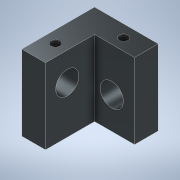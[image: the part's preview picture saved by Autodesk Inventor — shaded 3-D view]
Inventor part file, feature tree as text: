
AUTODESK INVENTOR PART (.ipt)
format: ipt  version: 2021 (Build 250183000, 183)  size: 216,576 bytes
history: native  units: in
note: dims shown in document units (in); Inventor stores cm internally (conversion verified against a paired STEP export)
features: extrude x8, other x8, sketch x3, thread x2, plane x2, chamfer x1, fillet x1, projected_geometry x1
ambient origin geometry x8: Origin, YZ Plane, XZ Plane, XY Plane, X Axis, Y Axis, Z Axis, Center Point
bodies: Solid1 (feature_tree), Body (feature_tree), Solid2 (feature_tree)
feature tree (26):
  extrude  "Extrusion1"  Depth=1.378in
  other  "Lower Galvo Mount"
  other  "Upper Galvo Mount"
  extrude  "Extrusion2"  Depth=0.5118in
  extrude  "Extrusion3"  Depth=0.1969in
  extrude  "Extrusion4"  Depth=0.1969in
  extrude  "Extrusion5"  Depth=0.1969in
  thread  "Thread1"  [1 undecoded]
  thread  "Thread2"  [1 undecoded]
  extrude  "Extrusion6"  Depth=0.1969in
  other  "PCB Mount"
  extrude  "Extrusion7"  Depth=0.1969in
  extrude  "Extrusion8"  Depth=0.1969in
  chamfer  "Chamfer1"  [1 undecoded]
  fillet  "Fillet1"  Radius=1.6339in
  other  "Work Axis1"
  other  "Work Axis2"
  other  "xaxisplane"
  other  "yaxisplane"
  other  "projection plane"
  sketch  "Sketch6"  dims[d2=0.5118in d3=0.5118in]
  plane  "Work Plane5"
  sketch  "Sketch8"  dims[d4=0.1969in d5=0.1969in d6=1.1024in d7=0.8858in d8=1.6339in d9=0.0in d10=0.689in d11=0.502in d12=0.502in d13=1.0236in d14=0.0in d15=0.0in d16=1.6339in d17=0.0in d18=1.6339in d19=0.0in d20=0.714in d21=0.0in d22=1.6339in d23=0.0in d24=0.3794in d25=0.0in d26=1.1024in d27=0.6102in d28=1.1417in d29=0.1378in d30=0.1378in d31=0.1378in d32=0.1969in d33=0.3937in d34=0.0in d35=1.378in d36=1.5748in d37=0.5118in d38=4.7244in d39=0.1969in d40=0.0984in d41=0.0984in d42=0.0984in d43=0.0in d44=0.1969in d45=0.0in d46=0.2165in d47=0.0886in d48=0.0787in d49=45.0deg d50=0.1969in d51=0.3436in d52=0.3436in d53=0.0in d54=3.937in d55=3.937in d57=90.0deg d59=0.6871in d60=0.5497in]
  sketch  "Sketch4"  dims[d0=1.5748in d1=1.378in]
  plane  "Work Plane3"
  projected_geometry  "Project Cut Edges1"
note: 3 required parameter values undecoded (feature->parameter linkage not recoverable at this tier; creation-order binding heuristic only, values carry confidence <= 0.55)
